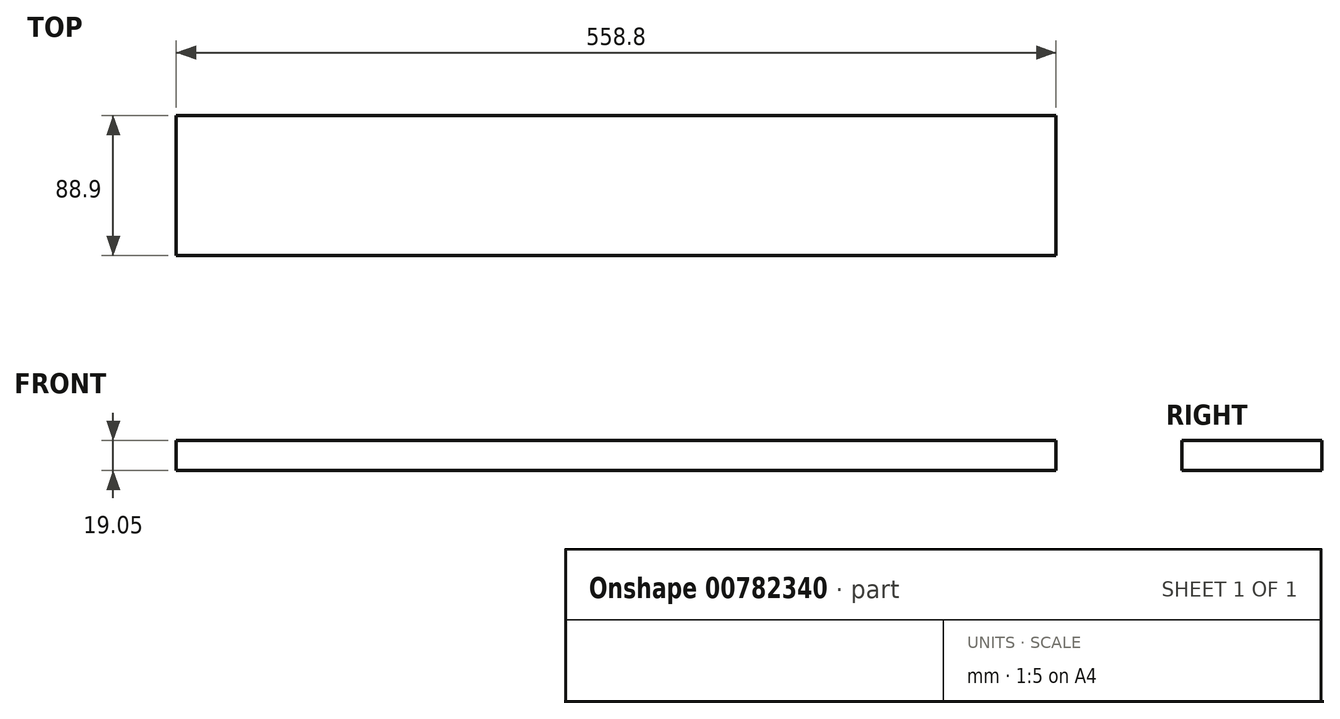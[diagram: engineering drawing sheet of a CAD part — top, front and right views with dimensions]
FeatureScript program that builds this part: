
annotation { "Feature Type Name" : "Feature", "Feature Type Description" : "" }
export const myFeature = defineFeature(function(context is Context, id is Id, definition is map)
    precondition{}
    {
        {
            var Q0;
            Q0=qCreatedBy(makeId("Top.planeOp"),FACE);
            var sketch = newSketch(context, id + "F0", { "sketchPlane" : qUnion([Q0])});
            skLineSegment(sketch, "E0.bottom", {"start": v(279.4, -44.45) * mm, "end": v(-279.4, -44.45) * mm});
            skLineSegment(sketch, "E0.top", {"start": v(279.4, 44.45) * mm, "end": v(-279.4, 44.45) * mm});
            skLineSegment(sketch, "E0.left", {"start": v(279.4, -44.45) * mm, "end": v(279.4, 44.45) * mm});
            skLineSegment(sketch, "E0.right", {"start": v(-279.4, -44.45) * mm, "end": v(-279.4, 44.45) * mm});
            skPoint(sketch, "E0.middle", {"position": v(0, 0) * mm});
            skSolve(sketch);
        }
        {
            var Q0;
            Q0 = qSketchRegion(id + "F0", true);
            extrude(context, id + "F1", {"entities" : qUnion([Q0]), "depth" : 19.05 * mm, "offsetDistance" : 25.4 * mm});
        }
    });
